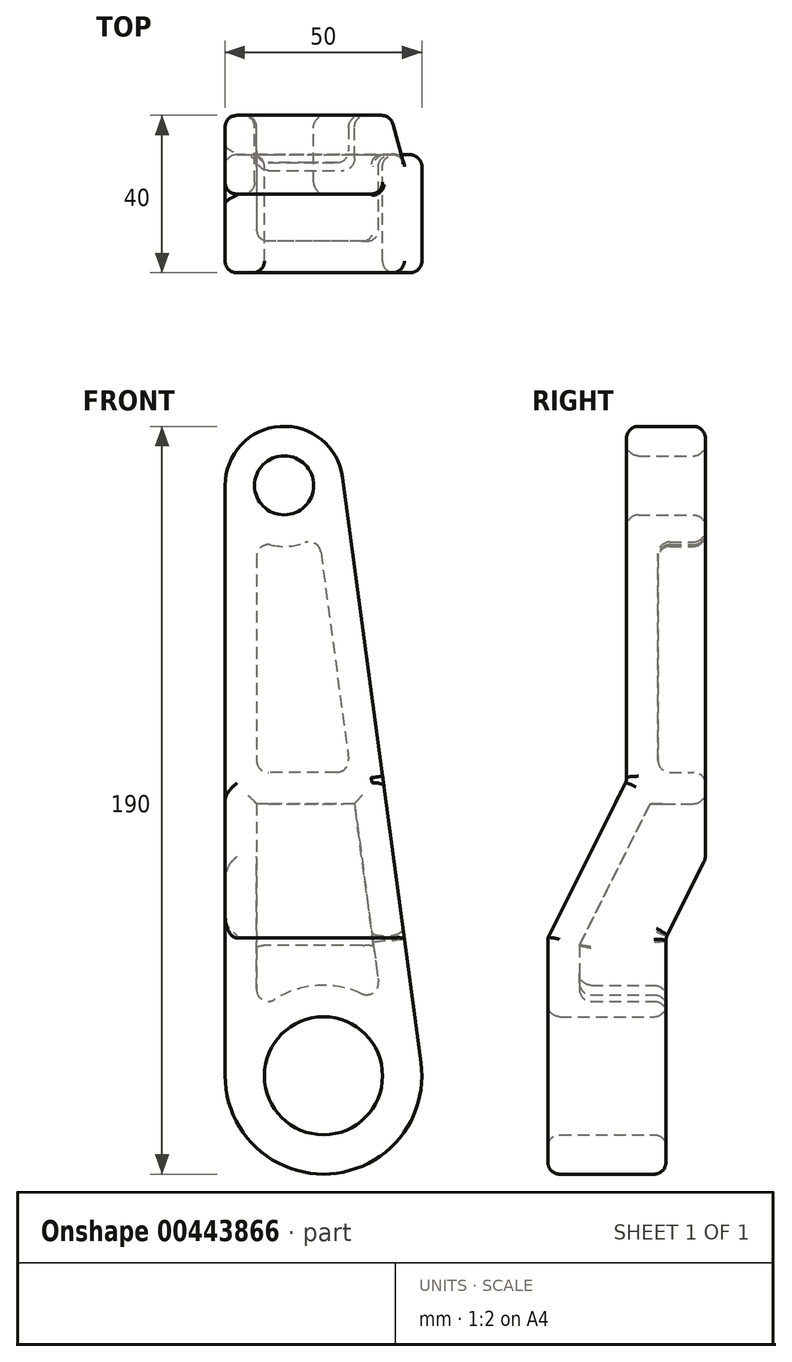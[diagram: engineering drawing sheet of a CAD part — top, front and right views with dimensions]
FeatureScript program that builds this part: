
annotation { "Feature Type Name" : "Feature", "Feature Type Description" : "" }
export const myFeature = defineFeature(function(context is Context, id is Id, definition is map)
    precondition{}
    {
        {
            var Q0;
            Q0=qCreatedBy(makeId("Front.planeOp"),FACE);
            var sketch = newSketch(context, id + "F0", { "sketchPlane" : qUnion([Q0])});
            skCircle(sketch, "E0", {"center": v(0, 0) * mm, "radius": 25 * mm});
            skCircle(sketch, "E1", {"center": v(-10, 150) * mm, "radius": 15 * mm});
            skLineSegment(sketch, "E2", {"start": v(-25, 150) * mm, "end": v(-25, 0) * mm});
            skLineSegment(sketch, "E3", {"start": v(4.87, 152) * mm, "end": v(24.78, 3.32) * mm});
            skPoint(sketch, "E4.orphan", {"position": v(0, 188.33) * mm});
            skSolve(sketch);
        }
        {
            var Q0;
            Q0 = qSketchRegion(id + "F0", true);
            extrude(context, id + "F1", {"entities" : qUnion([Q0]), "depth" : 40 * mm});
        }
        {
            var Q0;
            Q0=makeQuery(id+"F1.opExtrude","SWEPT_FACE",FACE,{"disambiguationData":[OSD([sQuery(id+"F0.wireOp",EDGE,"E2")])]});
            var sketch = newSketch(context, id + "F2", { "sketchPlane" : qUnion([Q0])});
            skLineSegment(sketch, "E5", {"start": v(20, 179.1) * mm, "end": v(20, 75) * mm});
            skLineSegment(sketch, "E6", {"start": v(20, 75) * mm, "end": v(40, 35) * mm});
            skLineSegment(sketch, "E7", {"start": v(40, 35) * mm, "end": v(40, 179.1) * mm});
            skLineSegment(sketch, "E8", {"start": v(0, 55) * mm, "end": v(0, 3.71) * mm});
            skLineSegment(sketch, "E9", {"start": v(0, 3.71) * mm, "end": v(0, -38.67) * mm});
            skLineSegment(sketch, "E10", {"start": v(10, -38.67) * mm, "end": v(10, 35) * mm});
            skLineSegment(sketch, "E11", {"start": v(10, 35) * mm, "end": v(0, 55) * mm});
            skLineSegment(sketch, "E12", {"start": v(20, 179.1) * mm, "end": v(40, 179.1) * mm});
            skLineSegment(sketch, "E13", {"start": v(0, -38.67) * mm, "end": v(10, -38.67) * mm});
            skSolve(sketch);
        }
        {
            var Q0;
            Q0 = qSketchRegion(id + "F2", true);
            extrude(context, id + "F3", {"entities" : qUnion([Q0]), "operationType" : NewBodyOperationType.REMOVE, "endBound" : BoundingType.THROUGH_ALL, "oppositeDirection" : true, "depth" : 25 * mm});
        }
        {
            var Q0;
            Q0=makeQuery(id+"F1.opExtrude","CAP_FACE",FACE,{"disambiguationData":[OSD([sQuery(id+"F0.wireOp",EDGE,"E0"),sQuery(id+"F0.wireOp",EDGE,"E1"),sQuery(id+"F0.wireOp",EDGE,"E2"),sQuery(id+"F0.wireOp",EDGE,"E3")])],"isStart":true});
            var sketch = newSketch(context, id + "F4", { "sketchPlane" : qUnion([Q0])});
            skCircle(sketch, "E14", {"center": v(10, 150) * mm, "radius": 7.5 * mm});
            skCircle(sketch, "E15", {"center": v(0, 0) * mm, "radius": 15 * mm});
            skSolve(sketch);
        }
        {
            var Q0;
            Q0 = qSketchRegion(id + "F4", true);
            extrude(context, id + "F5", {"entities" : qUnion([Q0]), "operationType" : NewBodyOperationType.REMOVE, "endBound" : BoundingType.THROUGH_ALL, "oppositeDirection" : true, "depth" : 25 * mm});
        }
        {
            var Q0;
            Q0=makeQuery(id+"F1.opExtrude","CAP_FACE",FACE,{"disambiguationData":[OSD([sQuery(id+"F0.wireOp",EDGE,"E0"),sQuery(id+"F0.wireOp",EDGE,"E1"),sQuery(id+"F0.wireOp",EDGE,"E2"),sQuery(id+"F0.wireOp",EDGE,"E3")])],"isStart":true});
            var Q1;
            Q1=makeQuery(id+"F3.boolean.opBoolean","COPY",FACE,{"derivedFrom":makeQuery(id+"F3.opExtrude","SWEPT_FACE",FACE,{"disambiguationData":[OSD([sQuery(id+"F2.wireOp",EDGE,"E11")])]})});
            var Q2;
            Q2=makeQuery(id+"F3.boolean.opBoolean","COPY",FACE,{"derivedFrom":makeQuery(id+"F3.opExtrude","SWEPT_FACE",FACE,{"disambiguationData":[OSD([sQuery(id+"F2.wireOp",EDGE,"E10")])]})});
            shell(context, id + "F6", {"entities" : qUnion([Q0, Q1, Q2]), "thickness" : 8 * mm});
        }
        {
            var Q0;
            Q0=makeQuery(id+"F1.opExtrude","CAP_FACE",FACE,{"disambiguationData":[OSD([sQuery(id+"F0.wireOp",EDGE,"E0"),sQuery(id+"F0.wireOp",EDGE,"E1"),sQuery(id+"F0.wireOp",EDGE,"E2"),sQuery(id+"F0.wireOp",EDGE,"E3")])],"isStart":true});
            var sketch = newSketch(context, id + "F7", { "sketchPlane" : qUnion([Q0])});
            skLineSegment(sketch, "E16", {"start": v(-6.82, 77.11) * mm, "end": v(17, 77.11) * mm});
            skLineSegment(sketch, "E17", {"start": v(-7.9, 69.11) * mm, "end": v(17, 69.11) * mm});
            skLineSegment(sketch, "E18.0", {"start": v(1.23, 137.22) * mm, "end": v(-9.79, 55) * mm});
            skLineSegment(sketch, "E18.1", {"start": v(17, 136.17) * mm, "end": v(17, 55) * mm});
            skSolve(sketch);
        }
        {
            var Q0;
            Q0 = qSketchRegion(id + "F7", true);
            extrude(context, id + "F8", {"entities" : qUnion([Q0]), "operationType" : NewBodyOperationType.ADD, "endBound" : BoundingType.UP_TO_NEXT, "oppositeDirection" : true, "depth" : 25 * mm});
        }
        {
            var Q0;
            Q0=makeQuery(id+"F6.opShell","OFFSET_FACE",FACE,{"disambiguationData":[OSD([sQuery(id+"F2.wireOp",EDGE,"E5")])]});
            var Q1;
            Q1=makeQuery(id+"F3.boolean.opBoolean","COPY",EDGE,{"derivedFrom":makeQuery(id+"F3.opExtrude","CAP_EDGE",EDGE,{"disambiguationData":[OSD([sQuery(id+"F2.wireOp",EDGE,"E5")])],"isStart":true})});
            var Q2;
            Q2=makeQuery(id+"F1.opExtrude","CAP_EDGE",EDGE,{"disambiguationData":[OSD([sQuery(id+"F0.wireOp",EDGE,"E3")])],"isStart":true});
            var Q3;
            Q3=makeQuery(id+"F1.opExtrude","CAP_EDGE",EDGE,{"disambiguationData":[OSD([sQuery(id+"F0.wireOp",EDGE,"E1")])],"isStart":true});
            var Q4;
            Q4=makeQuery(id+"F3.boolean.opBoolean","INTERSECT",EDGE,{"derivedFrom":[makeQuery(id+"F1.opExtrude","SWEPT_FACE",FACE,{"disambiguationData":[OSD([sQuery(id+"F0.wireOp",EDGE,"E1")])]}),makeQuery(id+"F3.opExtrude","SWEPT_FACE",FACE,{"disambiguationData":[OSD([sQuery(id+"F2.wireOp",EDGE,"E5")])]})]});
            var Q5;
            Q5=makeQuery(id+"F5.boolean.opBoolean","INTERSECT",EDGE,{"derivedFrom":[makeQuery(id+"F3.boolean.opBoolean","COPY",FACE,{"derivedFrom":makeQuery(id+"F3.opExtrude","SWEPT_FACE",FACE,{"disambiguationData":[OSD([sQuery(id+"F2.wireOp",EDGE,"E10")])]})}),makeQuery(id+"F5.opExtrude","SWEPT_FACE",FACE,{"disambiguationData":[OSD([sQuery(id+"F4.wireOp",EDGE,"E15")])]})]});
            var Q6;
            Q6=makeQuery(id+"F3.boolean.opBoolean","COPY",EDGE,{"derivedFrom":makeQuery(id+"F3.opExtrude","CAP_EDGE",EDGE,{"disambiguationData":[OSD([sQuery(id+"F2.wireOp",EDGE,"E6")])],"isStart":true})});
            var Q7;
            Q7=makeQuery(id+"F1.opExtrude","CAP_EDGE",EDGE,{"disambiguationData":[OSD([sQuery(id+"F0.wireOp",EDGE,"E2")])],"isStart":false});
            var Q8;
            Q8=makeQuery(id+"F3.boolean.opBoolean","COPY",EDGE,{"derivedFrom":makeQuery(id+"F3.opExtrude","CAP_EDGE",EDGE,{"disambiguationData":[OSD([sQuery(id+"F2.wireOp",EDGE,"E10")])],"isStart":true})});
            var Q9;
            Q9=makeQuery(id+"F1.opExtrude","CAP_EDGE",EDGE,{"disambiguationData":[OSD([sQuery(id+"F0.wireOp",EDGE,"E3")])],"isStart":false});
            var Q10;
            Q10=makeQuery(id+"F1.opExtrude","CAP_EDGE",EDGE,{"disambiguationData":[OSD([sQuery(id+"F0.wireOp",EDGE,"E0")])],"isStart":false});
            var Q11;
            Q11=makeQuery(id+"F3.boolean.opBoolean","INTERSECT",EDGE,{"derivedFrom":[makeQuery(id+"F1.opExtrude","SWEPT_FACE",FACE,{"disambiguationData":[OSD([sQuery(id+"F0.wireOp",EDGE,"E3")])]}),makeQuery(id+"F3.opExtrude","SWEPT_FACE",FACE,{"disambiguationData":[OSD([sQuery(id+"F2.wireOp",EDGE,"E6")])]})]});
            var Q12;
            Q12=makeQuery(id+"F5.boolean.opBoolean","INTERSECT",EDGE,{"derivedFrom":[makeQuery(id+"F1.opExtrude","CAP_FACE",FACE,{"disambiguationData":[OSD([sQuery(id+"F0.wireOp",EDGE,"E0"),sQuery(id+"F0.wireOp",EDGE,"E1"),sQuery(id+"F0.wireOp",EDGE,"E2"),sQuery(id+"F0.wireOp",EDGE,"E3")])],"isStart":false}),makeQuery(id+"F5.opExtrude","SWEPT_FACE",FACE,{"disambiguationData":[OSD([sQuery(id+"F4.wireOp",EDGE,"E15")])]})]});
            var Q13;
            Q13=makeQuery(id+"F3.boolean.opBoolean","INTERSECT",EDGE,{"derivedFrom":[makeQuery(id+"F1.opExtrude","SWEPT_FACE",FACE,{"disambiguationData":[OSD([sQuery(id+"F0.wireOp",EDGE,"E0")])]}),makeQuery(id+"F3.opExtrude","SWEPT_FACE",FACE,{"disambiguationData":[OSD([sQuery(id+"F2.wireOp",EDGE,"E10")])]})]});
            var Q14;
            Q14=makeQuery(id+"F5.boolean.opBoolean","INTERSECT",EDGE,{"derivedFrom":[makeQuery(id+"F3.boolean.opBoolean","COPY",FACE,{"derivedFrom":makeQuery(id+"F3.opExtrude","SWEPT_FACE",FACE,{"disambiguationData":[OSD([sQuery(id+"F2.wireOp",EDGE,"E5")])]})}),makeQuery(id+"F5.opExtrude","SWEPT_FACE",FACE,{"disambiguationData":[OSD([sQuery(id+"F4.wireOp",EDGE,"E14")])]})]});
            var Q15;
            Q15=makeQuery(id+"F3.boolean.opBoolean","INTERSECT",EDGE,{"derivedFrom":[makeQuery(id+"F1.opExtrude","SWEPT_FACE",FACE,{"disambiguationData":[OSD([sQuery(id+"F0.wireOp",EDGE,"E3")])]}),makeQuery(id+"F3.opExtrude","SWEPT_FACE",FACE,{"disambiguationData":[OSD([sQuery(id+"F2.wireOp",EDGE,"E5")])]})]});
            var Q16;
            Q16=makeQuery(id+"F1.opExtrude","CAP_EDGE",EDGE,{"disambiguationData":[OSD([sQuery(id+"F0.wireOp",EDGE,"E2")])],"isStart":true});
            var Q17;
            Q17=makeQuery(id+"F3.boolean.opBoolean","COPY",EDGE,{"derivedFrom":makeQuery(id+"F3.opExtrude","SWEPT_EDGE",EDGE,{"disambiguationData":[OSD([sQuery(id+"F2.wireOp",EDGE,"E5"),sQuery(id+"F2.wireOp",EDGE,"E6")])]})});
            var Q18;
            Q18=makeQuery(id+"F3.boolean.opBoolean","COPY",EDGE,{"derivedFrom":makeQuery(id+"F3.opExtrude","SWEPT_EDGE",EDGE,{"disambiguationData":[OSD([sQuery(id+"F0.wireOp",EDGE,"E2"),sQuery(id+"F2.wireOp",EDGE,"E6"),sQuery(id+"F2.wireOp",EDGE,"E7")])]})});
            var Q19;
            Q19=makeQuery(id+"F3.boolean.opBoolean","COPY",EDGE,{"derivedFrom":makeQuery(id+"F3.opExtrude","CAP_EDGE",EDGE,{"disambiguationData":[OSD([sQuery(id+"F2.wireOp",EDGE,"E11")])],"isStart":true})});
            var Q20;
            Q20=makeQuery(id+"F5.boolean.opBoolean","COPY",EDGE,{"derivedFrom":makeQuery(id+"F5.opExtrude","CAP_EDGE",EDGE,{"disambiguationData":[OSD([sQuery(id+"F4.wireOp",EDGE,"E14")])],"isStart":true})});
            var Q21;
            Q21=makeQuery(id+"F6.opShell","OFFSET_EDGE",EDGE,{"disambiguationData":[OSD([sQuery(id+"F2.wireOp",EDGE,"E5")])]});
            var Q22;
            Q22=makeQuery(id+"F3.boolean.opBoolean","INTERSECT",EDGE,{"derivedFrom":[makeQuery(id+"F1.opExtrude","SWEPT_FACE",FACE,{"disambiguationData":[OSD([sQuery(id+"F0.wireOp",EDGE,"E3")])]}),makeQuery(id+"F3.opExtrude","SWEPT_FACE",FACE,{"disambiguationData":[OSD([sQuery(id+"F2.wireOp",EDGE,"E10")])]})]});
            var Q23;
            Q23=makeQuery(id+"F6.opShell","OFFSET_EDGE",EDGE,{"disambiguationData":[OSD([sQuery(id+"F2.wireOp",EDGE,"E6")])]});
            var Q24;
            Q24=makeQuery(id+"F6.opShell","OFFSET_EDGE",EDGE,{"disambiguationData":[OSD([sQuery(id+"F0.wireOp",EDGE,"E2"),sQuery(id+"F2.wireOp",EDGE,"E6"),sQuery(id+"F2.wireOp",EDGE,"E7")])]});
            var Q25;
            Q25=makeQuery(id+"F6.opShell","OFFSET_EDGE",EDGE,{"disambiguationData":[OSD([sQuery(id+"F2.wireOp",EDGE,"E10"),sQuery(id+"F2.wireOp",EDGE,"E11")])]});
            var Q26;
            Q26=makeQuery(id+"F6.opShell","OFFSET_EDGE",EDGE,{"disambiguationData":[OSD([sQuery(id+"F0.wireOp",EDGE,"E2"),sQuery(id+"F2.wireOp",EDGE,"E8"),sQuery(id+"F2.wireOp",EDGE,"E11")])]});
            var Q27;
            Q27=makeQuery(id+"F8.opExtrude","CAP_EDGE",EDGE,{"disambiguationData":[OSD([sQuery(id+"F7.wireOp",EDGE,"E16")])],"isStart":true});
            var Q28;
            Q28=makeQuery(id+"F6.opShell","OFFSET_EDGE",EDGE,{"disambiguationData":[OSD([sQuery(id+"F2.wireOp",EDGE,"E10")])]});
            var Q29;
            Q29=makeQuery(id+"F6.opShell","OFFSET_EDGE",EDGE,{"disambiguationData":[OSD([sQuery(id+"F2.wireOp",EDGE,"E11")])]});
            var Q30;
            {var subQ0=sQuery(id+"F0.wireOp",EDGE,"E2");Q30=makeQuery(id+"F6.opShell","OFFSET_EDGE",EDGE,{"disambiguationData":[OSD([subQ0]),TDD([makeQuery(id+"F1.opExtrude","CAP_EDGE",EDGE,{"disambiguationData":[OSD([subQ0])],"isStart":false})])]});}
            var Q31;
            Q31=makeQuery(id+"F6.opShell","OFFSET_EDGE",EDGE,{"disambiguationData":[OSD([sQuery(id+"F0.wireOp",EDGE,"E3"),sQuery(id+"F2.wireOp",EDGE,"E5")])]});
            var Q32;
            Q32=makeQuery(id+"F6.opShell","TWEAK_EDGE",EDGE,{"derivedFrom":[makeQuery(id+"F1.opExtrude","SWEPT_FACE",FACE,{"disambiguationData":[OSD([sQuery(id+"F0.wireOp",EDGE,"E2")])]}),makeQuery(id+"F5.boolean.opBoolean","COPY",FACE,{"derivedFrom":makeQuery(id+"F5.opExtrude","SWEPT_FACE",FACE,{"disambiguationData":[OSD([sQuery(id+"F4.wireOp",EDGE,"E15")])]})})]});
            var Q33;
            Q33=makeQuery(id+"F6.opShell","TWEAK_EDGE",EDGE,{"derivedFrom":[makeQuery(id+"F1.opExtrude","SWEPT_FACE",FACE,{"disambiguationData":[OSD([sQuery(id+"F0.wireOp",EDGE,"E3")])]}),makeQuery(id+"F5.boolean.opBoolean","COPY",FACE,{"derivedFrom":makeQuery(id+"F5.opExtrude","SWEPT_FACE",FACE,{"disambiguationData":[OSD([sQuery(id+"F4.wireOp",EDGE,"E15")])]})})]});
            var Q34;
            Q34=makeQuery(id+"F6.opShell","OFFSET_EDGE",EDGE,{"disambiguationData":[OSD([sQuery(id+"F2.wireOp",EDGE,"E5"),sQuery(id+"F4.wireOp",EDGE,"E14")])]});
            var Q35;
            Q35=makeQuery(id+"F6.opShell","OFFSET_EDGE",EDGE,{"disambiguationData":[OSD([sQuery(id+"F0.wireOp",EDGE,"E0"),sQuery(id+"F0.wireOp",EDGE,"E1"),sQuery(id+"F0.wireOp",EDGE,"E2"),sQuery(id+"F0.wireOp",EDGE,"E3"),sQuery(id+"F4.wireOp",EDGE,"E15")])]});
            var Q36;
            Q36=makeQuery(id+"F6.opShell","OFFSET_EDGE",EDGE,{"disambiguationData":[OSD([sQuery(id+"F0.wireOp",EDGE,"E3"),sQuery(id+"F2.wireOp",EDGE,"E6")])]});
            var Q37;
            Q37=makeQuery(id+"F8.opExtrude","CAP_EDGE",EDGE,{"disambiguationData":[OSD([sQuery(id+"F7.wireOp",EDGE,"E16")])],"isStart":false});
            var Q38;
            Q38=makeQuery(id+"F8.opExtrude","SWEPT_EDGE",EDGE,{"disambiguationData":[OSD([sQuery(id+"F7.wireOp",EDGE,"E17"),sQuery(id+"F7.wireOp",EDGE,"E18.1")])]});
            var Q39;
            {var subQ1=sQuery(id+"F0.wireOp",EDGE,"E2");Q39=makeQuery(id+"F8.boolean.opBoolean","SPLIT",EDGE,{"disambiguationData":[TD([makeQuery(id+"F3.boolean.opBoolean","COPY",FACE,{"derivedFrom":makeQuery(id+"F3.opExtrude","SWEPT_FACE",FACE,{"disambiguationData":[OSD([sQuery(id+"F2.wireOp",EDGE,"E11")])]})})])],"derivedFrom":makeQuery(id+"F6.opShell","OFFSET_EDGE",EDGE,{"disambiguationData":[OSD([subQ1]),TDD([makeQuery(id+"F1.opExtrude","CAP_EDGE",EDGE,{"disambiguationData":[OSD([subQ1])],"isStart":true})])]})});}
            var Q40;
            Q40=makeQuery(id+"F6.opShell","OFFSET_EDGE",EDGE,{"disambiguationData":[OSD([sQuery(id+"F0.wireOp",EDGE,"E3"),sQuery(id+"F2.wireOp",EDGE,"E11")])]});
            var Q41;
            Q41=makeQuery(id+"F6.opShell","OFFSET_EDGE",EDGE,{"disambiguationData":[OSD([sQuery(id+"F0.wireOp",EDGE,"E3"),sQuery(id+"F2.wireOp",EDGE,"E10")])]});
            var Q42;
            Q42=makeQuery(id+"F8.opExtrude","CAP_EDGE",EDGE,{"disambiguationData":[OSD([sQuery(id+"F7.wireOp",EDGE,"E17")])],"isStart":true});
            var Q43;
            {var subQ0=sQuery(id+"F0.wireOp",EDGE,"E3");Q43=makeQuery(id+"F6.opShell","OFFSET_EDGE",EDGE,{"disambiguationData":[OSD([subQ0]),TDD([makeQuery(id+"F1.opExtrude","CAP_EDGE",EDGE,{"disambiguationData":[OSD([subQ0])],"isStart":false})])]});}
            var Q44;
            Q44=makeQuery(id+"F6.opShell","TWEAK_EDGE",EDGE,{"derivedFrom":[makeQuery(id+"F1.opExtrude","SWEPT_FACE",FACE,{"disambiguationData":[OSD([sQuery(id+"F0.wireOp",EDGE,"E2")])]}),makeQuery(id+"F5.boolean.opBoolean","COPY",FACE,{"derivedFrom":makeQuery(id+"F5.opExtrude","SWEPT_FACE",FACE,{"disambiguationData":[OSD([sQuery(id+"F4.wireOp",EDGE,"E14")])]})})]});
            var Q45;
            Q45=makeQuery(id+"F6.opShell","TWEAK_EDGE",EDGE,{"derivedFrom":[makeQuery(id+"F1.opExtrude","SWEPT_FACE",FACE,{"disambiguationData":[OSD([sQuery(id+"F0.wireOp",EDGE,"E3")])]}),makeQuery(id+"F5.boolean.opBoolean","COPY",FACE,{"derivedFrom":makeQuery(id+"F5.opExtrude","SWEPT_FACE",FACE,{"disambiguationData":[OSD([sQuery(id+"F4.wireOp",EDGE,"E14")])]})})]});
            var Q46;
            Q46=makeQuery(id+"F6.opShell","OFFSET_EDGE",EDGE,{"disambiguationData":[OSD([sQuery(id+"F4.wireOp",EDGE,"E14")])]});
            var Q47;
            Q47=makeQuery(id+"F6.opShell","OFFSET_EDGE",EDGE,{"disambiguationData":[OSD([sQuery(id+"F2.wireOp",EDGE,"E10"),sQuery(id+"F4.wireOp",EDGE,"E15")])]});
            var Q48;
            Q48=makeQuery(id+"F8.opExtrude","CAP_EDGE",EDGE,{"disambiguationData":[OSD([sQuery(id+"F7.wireOp",EDGE,"E17")])],"isStart":false});
            var Q49;
            Q49=makeQuery(id+"F8.opExtrude","SWEPT_EDGE",EDGE,{"disambiguationData":[OSD([sQuery(id+"F7.wireOp",EDGE,"E16"),sQuery(id+"F7.wireOp",EDGE,"E18.0")])]});
            var Q50;
            Q50=makeQuery(id+"F8.opExtrude","SWEPT_EDGE",EDGE,{"disambiguationData":[OSD([sQuery(id+"F7.wireOp",EDGE,"E16"),sQuery(id+"F7.wireOp",EDGE,"E18.1")])]});
            var Q51;
            Q51=makeQuery(id+"F8.opExtrude","SWEPT_EDGE",EDGE,{"disambiguationData":[OSD([sQuery(id+"F7.wireOp",EDGE,"E17"),sQuery(id+"F7.wireOp",EDGE,"E18.0")])]});
            var Q52;
            {var subQ1=sQuery(id+"F0.wireOp",EDGE,"E3");Q52=makeQuery(id+"F8.boolean.opBoolean","SPLIT",EDGE,{"disambiguationData":[TD([makeQuery(id+"F6.opShell","OFFSET_FACE",FACE,{"disambiguationData":[OSD([sQuery(id+"F2.wireOp",EDGE,"E11")])]})])],"derivedFrom":makeQuery(id+"F6.opShell","OFFSET_EDGE",EDGE,{"disambiguationData":[OSD([subQ1]),TDD([makeQuery(id+"F1.opExtrude","CAP_EDGE",EDGE,{"disambiguationData":[OSD([subQ1])],"isStart":true})])]})});}
            var Q53;
            Q53=makeQuery(id+"F3.boolean.opBoolean","INTERSECT",EDGE,{"derivedFrom":[makeQuery(id+"F1.opExtrude","SWEPT_FACE",FACE,{"disambiguationData":[OSD([sQuery(id+"F0.wireOp",EDGE,"E3")])]}),makeQuery(id+"F3.opExtrude","SWEPT_FACE",FACE,{"disambiguationData":[OSD([sQuery(id+"F2.wireOp",EDGE,"E11")])]})]});
            var Q54;
            Q54=makeQuery(id+"F3.boolean.opBoolean","COPY",EDGE,{"derivedFrom":makeQuery(id+"F3.opExtrude","SWEPT_EDGE",EDGE,{"disambiguationData":[OSD([sQuery(id+"F0.wireOp",EDGE,"E2"),sQuery(id+"F2.wireOp",EDGE,"E8"),sQuery(id+"F2.wireOp",EDGE,"E11")])]})});
            var Q55;
            Q55=makeQuery(id+"F3.boolean.opBoolean","COPY",EDGE,{"derivedFrom":makeQuery(id+"F3.opExtrude","SWEPT_EDGE",EDGE,{"disambiguationData":[OSD([sQuery(id+"F2.wireOp",EDGE,"E10"),sQuery(id+"F2.wireOp",EDGE,"E11")])]})});
            var Q56;
            Q56=makeQuery(id+"F8.boolean.opBoolean","MERGE",FACE,{"derivedFrom":[makeQuery(id+"F1.opExtrude","CAP_FACE",FACE,{"disambiguationData":[OSD([sQuery(id+"F0.wireOp",EDGE,"E0"),sQuery(id+"F0.wireOp",EDGE,"E1"),sQuery(id+"F0.wireOp",EDGE,"E2"),sQuery(id+"F0.wireOp",EDGE,"E3")])],"isStart":true}),makeQuery(id+"F8.opExtrude","CAP_FACE",FACE,{"disambiguationData":[OSD([sQuery(id+"F7.wireOp",EDGE,"E16"),sQuery(id+"F7.wireOp",EDGE,"E17"),sQuery(id+"F7.wireOp",EDGE,"E18.0"),sQuery(id+"F7.wireOp",EDGE,"E18.1")])],"isStart":true})]});
            var Q57;
            {var subQ1=sQuery(id+"F0.wireOp",EDGE,"E3");Q57=makeQuery(id+"F8.boolean.opBoolean","SPLIT",EDGE,{"disambiguationData":[TD([makeQuery(id+"F6.opShell","OFFSET_FACE",FACE,{"disambiguationData":[OSD([sQuery(id+"F4.wireOp",EDGE,"E14")])]})])],"derivedFrom":makeQuery(id+"F6.opShell","OFFSET_EDGE",EDGE,{"disambiguationData":[OSD([subQ1]),TDD([makeQuery(id+"F1.opExtrude","CAP_EDGE",EDGE,{"disambiguationData":[OSD([subQ1])],"isStart":true})])]})});}
            var Q58;
            {var subQ1=sQuery(id+"F0.wireOp",EDGE,"E2");Q58=makeQuery(id+"F8.boolean.opBoolean","SPLIT",EDGE,{"disambiguationData":[TD([makeQuery(id+"F6.opShell","OFFSET_FACE",FACE,{"disambiguationData":[OSD([sQuery(id+"F4.wireOp",EDGE,"E14")])]})])],"derivedFrom":makeQuery(id+"F6.opShell","OFFSET_EDGE",EDGE,{"disambiguationData":[OSD([subQ1]),TDD([makeQuery(id+"F1.opExtrude","CAP_EDGE",EDGE,{"disambiguationData":[OSD([subQ1])],"isStart":true})])]})});}
            fillet(context, id + "F9", {"entities" : qUnion([Q0, Q1, Q2, Q3, Q4, Q5, Q6, Q7, Q8, Q9, Q10, Q11, Q12, Q13, Q14, Q15, Q16, Q17, Q18, Q19, Q20, Q21, Q22, Q23, Q24, Q25, Q26, Q27, Q28, Q29, Q30, Q31, Q32, Q33, Q34, Q35, Q36, Q37, Q38, Q39, Q40, Q41, Q42, Q43, Q44, Q45, Q46, Q47, Q48, Q49, Q50, Q51, Q52, Q53, Q54, Q55, Q56, Q57, Q58]), "radius" : 3 * mm, "tangentPropagation" : true, "allowEdgeOverflow" : false});
        }
    });
